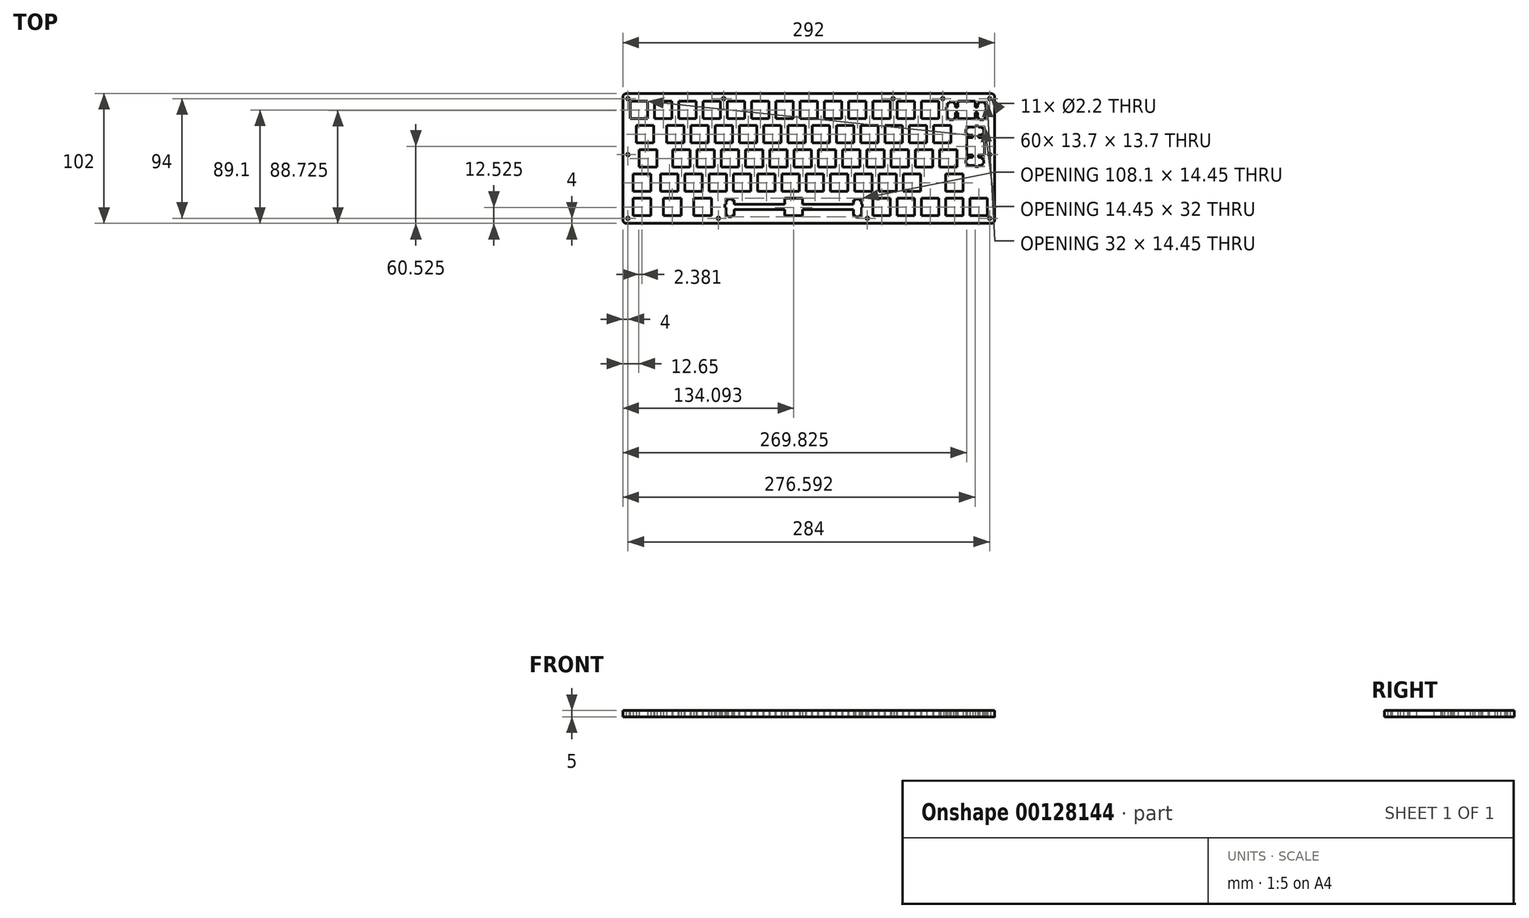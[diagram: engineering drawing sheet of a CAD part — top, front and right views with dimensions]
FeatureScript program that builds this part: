
annotation { "Feature Type Name" : "Feature", "Feature Type Description" : "" }
export const myFeature = defineFeature(function(context is Context, id is Id, definition is map)
    precondition{}
    {
        {
            var Q0;
            Q0=qCreatedBy(makeId("Top.planeOp"),FACE);
            var sketch = newSketch(context, id + "F0", { "sketchPlane" : qUnion([Q0])});
            skLineSegment(sketch, "E0", {"start": v(-18.76, -31.25) * mm, "end": v(-18.76, -35.95) * mm});
            skLineSegment(sketch, "E1", {"start": v(-18.76, -35.95) * mm, "end": v(-58.73, -35.95) * mm});
            skLineSegment(sketch, "E2", {"start": v(-58.73, -35.95) * mm, "end": v(-58.73, -32.72) * mm});
            skLineSegment(sketch, "E3", {"start": v(-58.73, -32.72) * mm, "end": v(-60.4, -32.72) * mm});
            skLineSegment(sketch, "E4", {"start": v(-60.4, -32.72) * mm, "end": v(-60.4, -31.8) * mm});
            skLineSegment(sketch, "E5", {"start": v(-60.4, -31.8) * mm, "end": v(-63.4, -31.8) * mm});
            skLineSegment(sketch, "E6", {"start": v(-63.4, -31.8) * mm, "end": v(-63.4, -32.72) * mm});
            skLineSegment(sketch, "E7", {"start": v(-63.4, -32.72) * mm, "end": v(-65.08, -32.72) * mm});
            skLineSegment(sketch, "E8", {"start": v(-65.08, -32.72) * mm, "end": v(-65.08, -35.95) * mm});
            skLineSegment(sketch, "E9", {"start": v(-65.08, -35.95) * mm, "end": v(-65.96, -35.95) * mm});
            skLineSegment(sketch, "E10", {"start": v(-65.96, -35.95) * mm, "end": v(-65.96, -38.45) * mm});
            skLineSegment(sketch, "E11", {"start": v(-65.96, -38.45) * mm, "end": v(-65.08, -38.45) * mm});
            skLineSegment(sketch, "E12", {"start": v(-65.08, -38.45) * mm, "end": v(-65.08, -44.72) * mm});
            skLineSegment(sketch, "E13", {"start": v(-65.08, -44.72) * mm, "end": v(-63.4, -44.72) * mm});
            skLineSegment(sketch, "E14", {"start": v(-63.4, -44.72) * mm, "end": v(-63.4, -45.7) * mm});
            skLineSegment(sketch, "E15", {"start": v(-63.4, -45.7) * mm, "end": v(-60.4, -45.7) * mm});
            skLineSegment(sketch, "E16", {"start": v(-60.4, -45.7) * mm, "end": v(-60.4, -44.72) * mm});
            skLineSegment(sketch, "E17", {"start": v(-60.4, -44.72) * mm, "end": v(-58.73, -44.72) * mm});
            skLineSegment(sketch, "E18", {"start": v(-58.73, -44.72) * mm, "end": v(-58.73, -40.25) * mm});
            skLineSegment(sketch, "E19", {"start": v(-58.73, -40.25) * mm, "end": v(-18.76, -40.25) * mm});
            skLineSegment(sketch, "E20", {"start": v(-18.76, -40.25) * mm, "end": v(-18.76, -44.95) * mm});
            skLineSegment(sketch, "E21", {"start": v(-18.76, -44.95) * mm, "end": v(-5.06, -44.95) * mm});
            skLineSegment(sketch, "E22", {"start": v(-5.06, -44.95) * mm, "end": v(-5.06, -40.25) * mm});
            skLineSegment(sketch, "E23", {"start": v(-5.06, -40.25) * mm, "end": v(34.92, -40.25) * mm});
            skLineSegment(sketch, "E24", {"start": v(34.92, -40.25) * mm, "end": v(34.92, -44.72) * mm});
            skLineSegment(sketch, "E25", {"start": v(34.92, -44.72) * mm, "end": v(36.6, -44.72) * mm});
            skLineSegment(sketch, "E26", {"start": v(36.6, -44.72) * mm, "end": v(36.6, -45.7) * mm});
            skLineSegment(sketch, "E27", {"start": v(36.6, -45.7) * mm, "end": v(39.6, -45.7) * mm});
            skLineSegment(sketch, "E28", {"start": v(39.6, -45.7) * mm, "end": v(39.6, -44.72) * mm});
            skLineSegment(sketch, "E29", {"start": v(39.6, -44.72) * mm, "end": v(41.27, -44.72) * mm});
            skLineSegment(sketch, "E30", {"start": v(41.27, -44.72) * mm, "end": v(41.27, -38.45) * mm});
            skLineSegment(sketch, "E31", {"start": v(41.27, -38.45) * mm, "end": v(42.14, -38.45) * mm});
            skLineSegment(sketch, "E32", {"start": v(42.14, -38.45) * mm, "end": v(42.14, -35.95) * mm});
            skLineSegment(sketch, "E33", {"start": v(42.14, -35.95) * mm, "end": v(41.27, -35.95) * mm});
            skLineSegment(sketch, "E34", {"start": v(41.27, -35.95) * mm, "end": v(41.27, -32.72) * mm});
            skLineSegment(sketch, "E35", {"start": v(41.27, -32.72) * mm, "end": v(39.6, -32.72) * mm});
            skLineSegment(sketch, "E36", {"start": v(39.6, -32.72) * mm, "end": v(39.6, -31.8) * mm});
            skLineSegment(sketch, "E37", {"start": v(39.6, -31.8) * mm, "end": v(36.6, -31.8) * mm});
            skLineSegment(sketch, "E38", {"start": v(36.6, -31.8) * mm, "end": v(36.6, -32.72) * mm});
            skLineSegment(sketch, "E39", {"start": v(36.6, -32.72) * mm, "end": v(34.92, -32.72) * mm});
            skLineSegment(sketch, "E40", {"start": v(34.92, -32.72) * mm, "end": v(34.92, -35.95) * mm});
            skLineSegment(sketch, "E41", {"start": v(34.92, -35.95) * mm, "end": v(-5.06, -35.95) * mm});
            skLineSegment(sketch, "E42", {"start": v(-5.06, -35.95) * mm, "end": v(-5.06, -31.25) * mm});
            skLineSegment(sketch, "E43", {"start": v(-5.06, -31.25) * mm, "end": v(-18.76, -31.25) * mm});
            skLineSegment(sketch, "E44", {"start": v(-137.82, -31.25) * mm, "end": v(-124.12, -31.25) * mm});
            skLineSegment(sketch, "E45", {"start": v(-124.12, -31.25) * mm, "end": v(-124.12, -44.95) * mm});
            skLineSegment(sketch, "E46", {"start": v(-124.12, -44.95) * mm, "end": v(-137.82, -44.95) * mm});
            skLineSegment(sketch, "E47", {"start": v(-137.82, -44.95) * mm, "end": v(-137.82, -31.25) * mm});
            skLineSegment(sketch, "E48", {"start": v(-114, -31.25) * mm, "end": v(-100.3, -31.25) * mm});
            skLineSegment(sketch, "E49", {"start": v(-100.3, -31.25) * mm, "end": v(-100.3, -44.95) * mm});
            skLineSegment(sketch, "E50", {"start": v(-100.3, -44.95) * mm, "end": v(-114, -44.95) * mm});
            skLineSegment(sketch, "E51", {"start": v(-114, -44.95) * mm, "end": v(-114, -31.25) * mm});
            skLineSegment(sketch, "E52", {"start": v(-90.2, -31.25) * mm, "end": v(-76.5, -31.25) * mm});
            skLineSegment(sketch, "E53", {"start": v(-76.5, -31.25) * mm, "end": v(-76.5, -44.95) * mm});
            skLineSegment(sketch, "E54", {"start": v(-76.5, -44.95) * mm, "end": v(-90.2, -44.95) * mm});
            skLineSegment(sketch, "E55", {"start": v(-90.2, -44.95) * mm, "end": v(-90.2, -31.25) * mm});
            skLineSegment(sketch, "E56", {"start": v(50.3, -31.25) * mm, "end": v(64, -31.25) * mm});
            skLineSegment(sketch, "E57", {"start": v(64, -31.25) * mm, "end": v(64, -44.95) * mm});
            skLineSegment(sketch, "E58", {"start": v(64, -44.95) * mm, "end": v(50.3, -44.95) * mm});
            skLineSegment(sketch, "E59", {"start": v(50.3, -44.95) * mm, "end": v(50.3, -31.25) * mm});
            skLineSegment(sketch, "E60", {"start": v(69.35, -31.25) * mm, "end": v(83.05, -31.25) * mm});
            skLineSegment(sketch, "E61", {"start": v(83.05, -31.25) * mm, "end": v(83.05, -44.95) * mm});
            skLineSegment(sketch, "E62", {"start": v(83.05, -44.95) * mm, "end": v(69.35, -44.95) * mm});
            skLineSegment(sketch, "E63", {"start": v(69.35, -44.95) * mm, "end": v(69.35, -31.25) * mm});
            skLineSegment(sketch, "E64", {"start": v(88.4, -31.25) * mm, "end": v(102.1, -31.25) * mm});
            skLineSegment(sketch, "E65", {"start": v(102.1, -31.25) * mm, "end": v(102.1, -44.95) * mm});
            skLineSegment(sketch, "E66", {"start": v(102.1, -44.95) * mm, "end": v(88.4, -44.95) * mm});
            skLineSegment(sketch, "E67", {"start": v(88.4, -44.95) * mm, "end": v(88.4, -31.25) * mm});
            skLineSegment(sketch, "E68", {"start": v(107.45, -31.25) * mm, "end": v(121.15, -31.25) * mm});
            skLineSegment(sketch, "E69", {"start": v(121.15, -31.25) * mm, "end": v(121.15, -44.95) * mm});
            skLineSegment(sketch, "E70", {"start": v(121.15, -44.95) * mm, "end": v(107.45, -44.95) * mm});
            skLineSegment(sketch, "E71", {"start": v(107.45, -44.95) * mm, "end": v(107.45, -31.25) * mm});
            skLineSegment(sketch, "E72", {"start": v(126.5, -31.25) * mm, "end": v(140.2, -31.25) * mm});
            skLineSegment(sketch, "E73", {"start": v(140.2, -31.25) * mm, "end": v(140.2, -44.95) * mm});
            skLineSegment(sketch, "E74", {"start": v(140.2, -44.95) * mm, "end": v(126.5, -44.95) * mm});
            skLineSegment(sketch, "E75", {"start": v(126.5, -44.95) * mm, "end": v(126.5, -31.25) * mm});
            skLineSegment(sketch, "E76", {"start": v(-137.82, -12.2) * mm, "end": v(-124.12, -12.2) * mm});
            skLineSegment(sketch, "E77", {"start": v(-124.12, -12.2) * mm, "end": v(-124.12, -25.9) * mm});
            skLineSegment(sketch, "E78", {"start": v(-124.12, -25.9) * mm, "end": v(-137.82, -25.9) * mm});
            skLineSegment(sketch, "E79", {"start": v(-137.82, -25.9) * mm, "end": v(-137.82, -12.2) * mm});
            skLineSegment(sketch, "E80", {"start": v(-116.39, -12.2) * mm, "end": v(-102.69, -12.2) * mm});
            skLineSegment(sketch, "E81", {"start": v(-102.69, -12.2) * mm, "end": v(-102.69, -25.9) * mm});
            skLineSegment(sketch, "E82", {"start": v(-102.69, -25.9) * mm, "end": v(-116.39, -25.9) * mm});
            skLineSegment(sketch, "E83", {"start": v(-116.39, -25.9) * mm, "end": v(-116.39, -12.2) * mm});
            skLineSegment(sketch, "E84", {"start": v(-97.34, -12.2) * mm, "end": v(-83.64, -12.2) * mm});
            skLineSegment(sketch, "E85", {"start": v(-83.64, -12.2) * mm, "end": v(-83.64, -25.9) * mm});
            skLineSegment(sketch, "E86", {"start": v(-83.64, -25.9) * mm, "end": v(-97.34, -25.9) * mm});
            skLineSegment(sketch, "E87", {"start": v(-97.34, -25.9) * mm, "end": v(-97.34, -12.2) * mm});
            skLineSegment(sketch, "E88", {"start": v(-78.29, -12.2) * mm, "end": v(-64.59, -12.2) * mm});
            skLineSegment(sketch, "E89", {"start": v(-64.59, -12.2) * mm, "end": v(-64.59, -25.9) * mm});
            skLineSegment(sketch, "E90", {"start": v(-64.59, -25.9) * mm, "end": v(-78.29, -25.9) * mm});
            skLineSegment(sketch, "E91", {"start": v(-78.29, -25.9) * mm, "end": v(-78.29, -12.2) * mm});
            skLineSegment(sketch, "E92", {"start": v(-59.24, -12.2) * mm, "end": v(-45.54, -12.2) * mm});
            skLineSegment(sketch, "E93", {"start": v(-45.54, -12.2) * mm, "end": v(-45.54, -25.9) * mm});
            skLineSegment(sketch, "E94", {"start": v(-45.54, -25.9) * mm, "end": v(-59.24, -25.9) * mm});
            skLineSegment(sketch, "E95", {"start": v(-59.24, -25.9) * mm, "end": v(-59.24, -12.2) * mm});
            skLineSegment(sketch, "E96", {"start": v(-40.19, -12.2) * mm, "end": v(-26.49, -12.2) * mm});
            skLineSegment(sketch, "E97", {"start": v(-26.49, -12.2) * mm, "end": v(-26.49, -25.9) * mm});
            skLineSegment(sketch, "E98", {"start": v(-26.49, -25.9) * mm, "end": v(-40.19, -25.9) * mm});
            skLineSegment(sketch, "E99", {"start": v(-40.19, -25.9) * mm, "end": v(-40.19, -12.2) * mm});
            skLineSegment(sketch, "E100", {"start": v(-21.14, -12.2) * mm, "end": v(-7.44, -12.2) * mm});
            skLineSegment(sketch, "E101", {"start": v(-7.44, -12.2) * mm, "end": v(-7.44, -25.9) * mm});
            skLineSegment(sketch, "E102", {"start": v(-7.44, -25.9) * mm, "end": v(-21.14, -25.9) * mm});
            skLineSegment(sketch, "E103", {"start": v(-21.14, -25.9) * mm, "end": v(-21.14, -12.2) * mm});
            skLineSegment(sketch, "E104", {"start": v(-2.09, -12.2) * mm, "end": v(11.61, -12.2) * mm});
            skLineSegment(sketch, "E105", {"start": v(11.61, -12.2) * mm, "end": v(11.61, -25.9) * mm});
            skLineSegment(sketch, "E106", {"start": v(11.61, -25.9) * mm, "end": v(-2.09, -25.9) * mm});
            skLineSegment(sketch, "E107", {"start": v(-2.09, -25.9) * mm, "end": v(-2.09, -12.2) * mm});
            skLineSegment(sketch, "E108", {"start": v(16.96, -12.2) * mm, "end": v(30.66, -12.2) * mm});
            skLineSegment(sketch, "E109", {"start": v(30.66, -12.2) * mm, "end": v(30.66, -25.9) * mm});
            skLineSegment(sketch, "E110", {"start": v(30.66, -25.9) * mm, "end": v(16.96, -25.9) * mm});
            skLineSegment(sketch, "E111", {"start": v(16.96, -25.9) * mm, "end": v(16.96, -12.2) * mm});
            skLineSegment(sketch, "E112", {"start": v(36.01, -12.2) * mm, "end": v(49.71, -12.2) * mm});
            skLineSegment(sketch, "E113", {"start": v(49.71, -12.2) * mm, "end": v(49.71, -25.9) * mm});
            skLineSegment(sketch, "E114", {"start": v(49.71, -25.9) * mm, "end": v(36.01, -25.9) * mm});
            skLineSegment(sketch, "E115", {"start": v(36.01, -25.9) * mm, "end": v(36.01, -12.2) * mm});
            skLineSegment(sketch, "E116", {"start": v(55.06, -12.2) * mm, "end": v(68.76, -12.2) * mm});
            skLineSegment(sketch, "E117", {"start": v(68.76, -12.2) * mm, "end": v(68.76, -25.9) * mm});
            skLineSegment(sketch, "E118", {"start": v(68.76, -25.9) * mm, "end": v(55.06, -25.9) * mm});
            skLineSegment(sketch, "E119", {"start": v(55.06, -25.9) * mm, "end": v(55.06, -12.2) * mm});
            skLineSegment(sketch, "E120", {"start": v(74.11, -12.2) * mm, "end": v(87.81, -12.2) * mm});
            skLineSegment(sketch, "E121", {"start": v(87.81, -12.2) * mm, "end": v(87.81, -25.9) * mm});
            skLineSegment(sketch, "E122", {"start": v(87.81, -25.9) * mm, "end": v(74.11, -25.9) * mm});
            skLineSegment(sketch, "E123", {"start": v(74.11, -25.9) * mm, "end": v(74.11, -12.2) * mm});
            skLineSegment(sketch, "E124", {"start": v(107.45, -12.2) * mm, "end": v(121.15, -12.2) * mm});
            skLineSegment(sketch, "E125", {"start": v(121.15, -12.2) * mm, "end": v(121.15, -25.9) * mm});
            skLineSegment(sketch, "E126", {"start": v(121.15, -25.9) * mm, "end": v(107.45, -25.9) * mm});
            skLineSegment(sketch, "E127", {"start": v(107.45, -25.9) * mm, "end": v(107.45, -12.2) * mm});
            skLineSegment(sketch, "E128", {"start": v(-133.06, 6.85) * mm, "end": v(-119.36, 6.85) * mm});
            skLineSegment(sketch, "E129", {"start": v(-119.36, 6.85) * mm, "end": v(-119.36, -6.85) * mm});
            skLineSegment(sketch, "E130", {"start": v(-119.36, -6.85) * mm, "end": v(-133.06, -6.85) * mm});
            skLineSegment(sketch, "E131", {"start": v(-133.06, -6.85) * mm, "end": v(-133.06, 6.85) * mm});
            skLineSegment(sketch, "E132", {"start": v(-106.86, 6.85) * mm, "end": v(-93.16, 6.85) * mm});
            skLineSegment(sketch, "E133", {"start": v(-93.16, 6.85) * mm, "end": v(-93.16, -6.85) * mm});
            skLineSegment(sketch, "E134", {"start": v(-93.16, -6.85) * mm, "end": v(-106.86, -6.85) * mm});
            skLineSegment(sketch, "E135", {"start": v(-106.86, -6.85) * mm, "end": v(-106.86, 6.85) * mm});
            skLineSegment(sketch, "E136", {"start": v(-87.81, 6.85) * mm, "end": v(-74.11, 6.85) * mm});
            skLineSegment(sketch, "E137", {"start": v(-74.11, 6.85) * mm, "end": v(-74.11, -6.85) * mm});
            skLineSegment(sketch, "E138", {"start": v(-74.11, -6.85) * mm, "end": v(-87.81, -6.85) * mm});
            skLineSegment(sketch, "E139", {"start": v(-87.81, -6.85) * mm, "end": v(-87.81, 6.85) * mm});
            skLineSegment(sketch, "E140", {"start": v(-68.76, 6.85) * mm, "end": v(-55.06, 6.85) * mm});
            skLineSegment(sketch, "E141", {"start": v(-55.06, 6.85) * mm, "end": v(-55.06, -6.85) * mm});
            skLineSegment(sketch, "E142", {"start": v(-55.06, -6.85) * mm, "end": v(-68.76, -6.85) * mm});
            skLineSegment(sketch, "E143", {"start": v(-68.76, -6.85) * mm, "end": v(-68.76, 6.85) * mm});
            skLineSegment(sketch, "E144", {"start": v(-49.71, 6.85) * mm, "end": v(-36.01, 6.85) * mm});
            skLineSegment(sketch, "E145", {"start": v(-36.01, 6.85) * mm, "end": v(-36.01, -6.85) * mm});
            skLineSegment(sketch, "E146", {"start": v(-36.01, -6.85) * mm, "end": v(-49.71, -6.85) * mm});
            skLineSegment(sketch, "E147", {"start": v(-49.71, -6.85) * mm, "end": v(-49.71, 6.85) * mm});
            skLineSegment(sketch, "E148", {"start": v(-30.66, 6.85) * mm, "end": v(-16.96, 6.85) * mm});
            skLineSegment(sketch, "E149", {"start": v(-16.96, 6.85) * mm, "end": v(-16.96, -6.85) * mm});
            skLineSegment(sketch, "E150", {"start": v(-16.96, -6.85) * mm, "end": v(-30.66, -6.85) * mm});
            skLineSegment(sketch, "E151", {"start": v(-30.66, -6.85) * mm, "end": v(-30.66, 6.85) * mm});
            skLineSegment(sketch, "E152", {"start": v(-11.61, 6.85) * mm, "end": v(2.09, 6.85) * mm});
            skLineSegment(sketch, "E153", {"start": v(2.09, 6.85) * mm, "end": v(2.09, -6.85) * mm});
            skLineSegment(sketch, "E154", {"start": v(2.09, -6.85) * mm, "end": v(-11.61, -6.85) * mm});
            skLineSegment(sketch, "E155", {"start": v(-11.61, -6.85) * mm, "end": v(-11.61, 6.85) * mm});
            skLineSegment(sketch, "E156", {"start": v(7.44, 6.85) * mm, "end": v(21.14, 6.85) * mm});
            skLineSegment(sketch, "E157", {"start": v(21.14, 6.85) * mm, "end": v(21.14, -6.85) * mm});
            skLineSegment(sketch, "E158", {"start": v(21.14, -6.85) * mm, "end": v(7.44, -6.85) * mm});
            skLineSegment(sketch, "E159", {"start": v(7.44, -6.85) * mm, "end": v(7.44, 6.85) * mm});
            skLineSegment(sketch, "E160", {"start": v(26.49, 6.85) * mm, "end": v(40.19, 6.85) * mm});
            skLineSegment(sketch, "E161", {"start": v(40.19, 6.85) * mm, "end": v(40.19, -6.85) * mm});
            skLineSegment(sketch, "E162", {"start": v(40.19, -6.85) * mm, "end": v(26.49, -6.85) * mm});
            skLineSegment(sketch, "E163", {"start": v(26.49, -6.85) * mm, "end": v(26.49, 6.85) * mm});
            skLineSegment(sketch, "E164", {"start": v(45.54, 6.85) * mm, "end": v(59.24, 6.85) * mm});
            skLineSegment(sketch, "E165", {"start": v(59.24, 6.85) * mm, "end": v(59.24, -6.85) * mm});
            skLineSegment(sketch, "E166", {"start": v(59.24, -6.85) * mm, "end": v(45.54, -6.85) * mm});
            skLineSegment(sketch, "E167", {"start": v(45.54, -6.85) * mm, "end": v(45.54, 6.85) * mm});
            skLineSegment(sketch, "E168", {"start": v(64.59, 6.85) * mm, "end": v(78.29, 6.85) * mm});
            skLineSegment(sketch, "E169", {"start": v(78.29, 6.85) * mm, "end": v(78.29, -6.85) * mm});
            skLineSegment(sketch, "E170", {"start": v(78.29, -6.85) * mm, "end": v(64.59, -6.85) * mm});
            skLineSegment(sketch, "E171", {"start": v(64.59, -6.85) * mm, "end": v(64.59, 6.85) * mm});
            skLineSegment(sketch, "E172", {"start": v(83.64, 6.85) * mm, "end": v(97.34, 6.85) * mm});
            skLineSegment(sketch, "E173", {"start": v(97.34, 6.85) * mm, "end": v(97.34, -6.85) * mm});
            skLineSegment(sketch, "E174", {"start": v(97.34, -6.85) * mm, "end": v(83.64, -6.85) * mm});
            skLineSegment(sketch, "E175", {"start": v(83.64, -6.85) * mm, "end": v(83.64, 6.85) * mm});
            skLineSegment(sketch, "E176", {"start": v(102.69, 6.85) * mm, "end": v(116.39, 6.85) * mm});
            skLineSegment(sketch, "E177", {"start": v(116.39, 6.85) * mm, "end": v(116.39, -6.85) * mm});
            skLineSegment(sketch, "E178", {"start": v(116.39, -6.85) * mm, "end": v(102.69, -6.85) * mm});
            skLineSegment(sketch, "E179", {"start": v(102.69, -6.85) * mm, "end": v(102.69, 6.85) * mm});
            skLineSegment(sketch, "E180", {"start": v(130.62, 25.53) * mm, "end": v(130.62, 24.65) * mm});
            skLineSegment(sketch, "E181", {"start": v(130.62, 24.65) * mm, "end": v(124.35, 24.65) * mm});
            skLineSegment(sketch, "E182", {"start": v(124.35, 24.65) * mm, "end": v(124.35, 22.97) * mm});
            skLineSegment(sketch, "E183", {"start": v(124.35, 22.97) * mm, "end": v(123.37, 22.97) * mm});
            skLineSegment(sketch, "E184", {"start": v(123.37, 22.97) * mm, "end": v(123.37, 19.98) * mm});
            skLineSegment(sketch, "E185", {"start": v(123.37, 19.98) * mm, "end": v(124.35, 19.98) * mm});
            skLineSegment(sketch, "E186", {"start": v(124.35, 19.98) * mm, "end": v(124.35, 18.3) * mm});
            skLineSegment(sketch, "E187", {"start": v(124.35, 18.3) * mm, "end": v(128.82, 18.3) * mm});
            skLineSegment(sketch, "E188", {"start": v(128.82, 18.3) * mm, "end": v(128.82, 16.38) * mm});
            skLineSegment(sketch, "E189", {"start": v(128.82, 16.38) * mm, "end": v(124.12, 16.38) * mm});
            skLineSegment(sketch, "E190", {"start": v(124.12, 16.38) * mm, "end": v(124.12, 2.68) * mm});
            skLineSegment(sketch, "E191", {"start": v(124.12, 2.68) * mm, "end": v(128.82, 2.68) * mm});
            skLineSegment(sketch, "E192", {"start": v(128.82, 2.68) * mm, "end": v(128.82, 0.75) * mm});
            skLineSegment(sketch, "E193", {"start": v(128.82, 0.75) * mm, "end": v(124.35, 0.75) * mm});
            skLineSegment(sketch, "E194", {"start": v(124.35, 0.75) * mm, "end": v(124.35, -0.92) * mm});
            skLineSegment(sketch, "E195", {"start": v(124.35, -0.92) * mm, "end": v(123.37, -0.92) * mm});
            skLineSegment(sketch, "E196", {"start": v(123.37, -0.92) * mm, "end": v(123.37, -3.92) * mm});
            skLineSegment(sketch, "E197", {"start": v(123.37, -3.92) * mm, "end": v(124.35, -3.92) * mm});
            skLineSegment(sketch, "E198", {"start": v(124.35, -3.92) * mm, "end": v(124.35, -5.6) * mm});
            skLineSegment(sketch, "E199", {"start": v(124.35, -5.6) * mm, "end": v(130.62, -5.6) * mm});
            skLineSegment(sketch, "E200", {"start": v(130.62, -5.6) * mm, "end": v(130.62, -6.48) * mm});
            skLineSegment(sketch, "E201", {"start": v(130.62, -6.48) * mm, "end": v(133.12, -6.48) * mm});
            skLineSegment(sketch, "E202", {"start": v(133.12, -6.48) * mm, "end": v(133.12, -5.6) * mm});
            skLineSegment(sketch, "E203", {"start": v(133.12, -5.6) * mm, "end": v(136.35, -5.6) * mm});
            skLineSegment(sketch, "E204", {"start": v(136.35, -5.6) * mm, "end": v(136.35, -3.92) * mm});
            skLineSegment(sketch, "E205", {"start": v(136.35, -3.92) * mm, "end": v(137.27, -3.92) * mm});
            skLineSegment(sketch, "E206", {"start": v(137.27, -3.92) * mm, "end": v(137.27, -0.92) * mm});
            skLineSegment(sketch, "E207", {"start": v(137.27, -0.92) * mm, "end": v(136.35, -0.92) * mm});
            skLineSegment(sketch, "E208", {"start": v(136.35, -0.92) * mm, "end": v(136.35, 0.75) * mm});
            skLineSegment(sketch, "E209", {"start": v(136.35, 0.75) * mm, "end": v(133.12, 0.75) * mm});
            skLineSegment(sketch, "E210", {"start": v(133.12, 0.75) * mm, "end": v(133.12, 2.68) * mm});
            skLineSegment(sketch, "E211", {"start": v(133.12, 2.68) * mm, "end": v(137.82, 2.68) * mm});
            skLineSegment(sketch, "E212", {"start": v(137.82, 2.68) * mm, "end": v(137.82, 16.38) * mm});
            skLineSegment(sketch, "E213", {"start": v(137.82, 16.38) * mm, "end": v(133.12, 16.38) * mm});
            skLineSegment(sketch, "E214", {"start": v(133.12, 16.38) * mm, "end": v(133.12, 18.3) * mm});
            skLineSegment(sketch, "E215", {"start": v(133.12, 18.3) * mm, "end": v(136.35, 18.3) * mm});
            skLineSegment(sketch, "E216", {"start": v(136.35, 18.3) * mm, "end": v(136.35, 19.98) * mm});
            skLineSegment(sketch, "E217", {"start": v(136.35, 19.98) * mm, "end": v(137.27, 19.98) * mm});
            skLineSegment(sketch, "E218", {"start": v(137.27, 19.98) * mm, "end": v(137.27, 22.97) * mm});
            skLineSegment(sketch, "E219", {"start": v(137.27, 22.97) * mm, "end": v(136.35, 22.97) * mm});
            skLineSegment(sketch, "E220", {"start": v(136.35, 22.97) * mm, "end": v(136.35, 24.65) * mm});
            skLineSegment(sketch, "E221", {"start": v(136.35, 24.65) * mm, "end": v(133.12, 24.65) * mm});
            skLineSegment(sketch, "E222", {"start": v(133.12, 24.65) * mm, "end": v(133.12, 25.53) * mm});
            skLineSegment(sketch, "E223", {"start": v(133.12, 25.53) * mm, "end": v(130.62, 25.53) * mm});
            skLineSegment(sketch, "E224", {"start": v(-135.44, 25.9) * mm, "end": v(-121.74, 25.9) * mm});
            skLineSegment(sketch, "E225", {"start": v(-121.74, 25.9) * mm, "end": v(-121.74, 12.2) * mm});
            skLineSegment(sketch, "E226", {"start": v(-121.74, 12.2) * mm, "end": v(-135.44, 12.2) * mm});
            skLineSegment(sketch, "E227", {"start": v(-135.44, 12.2) * mm, "end": v(-135.44, 25.9) * mm});
            skLineSegment(sketch, "E228", {"start": v(-111.63, 25.9) * mm, "end": v(-97.92, 25.9) * mm});
            skLineSegment(sketch, "E229", {"start": v(-97.92, 25.9) * mm, "end": v(-97.92, 12.2) * mm});
            skLineSegment(sketch, "E230", {"start": v(-97.92, 12.2) * mm, "end": v(-111.63, 12.2) * mm});
            skLineSegment(sketch, "E231", {"start": v(-111.63, 12.2) * mm, "end": v(-111.63, 25.9) * mm});
            skLineSegment(sketch, "E232", {"start": v(-92.58, 25.9) * mm, "end": v(-78.88, 25.9) * mm});
            skLineSegment(sketch, "E233", {"start": v(-78.88, 25.9) * mm, "end": v(-78.88, 12.2) * mm});
            skLineSegment(sketch, "E234", {"start": v(-78.88, 12.2) * mm, "end": v(-92.58, 12.2) * mm});
            skLineSegment(sketch, "E235", {"start": v(-92.58, 12.2) * mm, "end": v(-92.58, 25.9) * mm});
            skLineSegment(sketch, "E236", {"start": v(-73.53, 25.9) * mm, "end": v(-59.83, 25.9) * mm});
            skLineSegment(sketch, "E237", {"start": v(-59.83, 25.9) * mm, "end": v(-59.83, 12.2) * mm});
            skLineSegment(sketch, "E238", {"start": v(-59.83, 12.2) * mm, "end": v(-73.53, 12.2) * mm});
            skLineSegment(sketch, "E239", {"start": v(-73.53, 12.2) * mm, "end": v(-73.53, 25.9) * mm});
            skLineSegment(sketch, "E240", {"start": v(-54.48, 25.9) * mm, "end": v(-40.78, 25.9) * mm});
            skLineSegment(sketch, "E241", {"start": v(-40.78, 25.9) * mm, "end": v(-40.78, 12.2) * mm});
            skLineSegment(sketch, "E242", {"start": v(-40.78, 12.2) * mm, "end": v(-54.48, 12.2) * mm});
            skLineSegment(sketch, "E243", {"start": v(-54.48, 12.2) * mm, "end": v(-54.48, 25.9) * mm});
            skLineSegment(sketch, "E244", {"start": v(-35.42, 25.9) * mm, "end": v(-21.73, 25.9) * mm});
            skLineSegment(sketch, "E245", {"start": v(-21.73, 25.9) * mm, "end": v(-21.73, 12.2) * mm});
            skLineSegment(sketch, "E246", {"start": v(-21.73, 12.2) * mm, "end": v(-35.42, 12.2) * mm});
            skLineSegment(sketch, "E247", {"start": v(-35.42, 12.2) * mm, "end": v(-35.42, 25.9) * mm});
            skLineSegment(sketch, "E248", {"start": v(-16.37, 25.9) * mm, "end": v(-2.67, 25.9) * mm});
            skLineSegment(sketch, "E249", {"start": v(-2.67, 25.9) * mm, "end": v(-2.67, 12.2) * mm});
            skLineSegment(sketch, "E250", {"start": v(-2.67, 12.2) * mm, "end": v(-16.37, 12.2) * mm});
            skLineSegment(sketch, "E251", {"start": v(-16.37, 12.2) * mm, "end": v(-16.37, 25.9) * mm});
            skLineSegment(sketch, "E252", {"start": v(2.68, 25.9) * mm, "end": v(16.38, 25.9) * mm});
            skLineSegment(sketch, "E253", {"start": v(16.38, 25.9) * mm, "end": v(16.38, 12.2) * mm});
            skLineSegment(sketch, "E254", {"start": v(16.38, 12.2) * mm, "end": v(2.68, 12.2) * mm});
            skLineSegment(sketch, "E255", {"start": v(2.68, 12.2) * mm, "end": v(2.68, 25.9) * mm});
            skLineSegment(sketch, "E256", {"start": v(21.73, 25.9) * mm, "end": v(35.43, 25.9) * mm});
            skLineSegment(sketch, "E257", {"start": v(35.43, 25.9) * mm, "end": v(35.43, 12.2) * mm});
            skLineSegment(sketch, "E258", {"start": v(35.43, 12.2) * mm, "end": v(21.73, 12.2) * mm});
            skLineSegment(sketch, "E259", {"start": v(21.73, 12.2) * mm, "end": v(21.73, 25.9) * mm});
            skLineSegment(sketch, "E260", {"start": v(40.78, 25.9) * mm, "end": v(54.48, 25.9) * mm});
            skLineSegment(sketch, "E261", {"start": v(54.48, 25.9) * mm, "end": v(54.48, 12.2) * mm});
            skLineSegment(sketch, "E262", {"start": v(54.48, 12.2) * mm, "end": v(40.78, 12.2) * mm});
            skLineSegment(sketch, "E263", {"start": v(40.78, 12.2) * mm, "end": v(40.78, 25.9) * mm});
            skLineSegment(sketch, "E264", {"start": v(59.83, 25.9) * mm, "end": v(73.53, 25.9) * mm});
            skLineSegment(sketch, "E265", {"start": v(73.53, 25.9) * mm, "end": v(73.53, 12.2) * mm});
            skLineSegment(sketch, "E266", {"start": v(73.53, 12.2) * mm, "end": v(59.83, 12.2) * mm});
            skLineSegment(sketch, "E267", {"start": v(59.83, 12.2) * mm, "end": v(59.83, 25.9) * mm});
            skLineSegment(sketch, "E268", {"start": v(78.88, 25.9) * mm, "end": v(92.58, 25.9) * mm});
            skLineSegment(sketch, "E269", {"start": v(92.58, 25.9) * mm, "end": v(92.58, 12.2) * mm});
            skLineSegment(sketch, "E270", {"start": v(92.58, 12.2) * mm, "end": v(78.88, 12.2) * mm});
            skLineSegment(sketch, "E271", {"start": v(78.88, 12.2) * mm, "end": v(78.88, 25.9) * mm});
            skLineSegment(sketch, "E272", {"start": v(97.93, 25.9) * mm, "end": v(111.63, 25.9) * mm});
            skLineSegment(sketch, "E273", {"start": v(111.63, 25.9) * mm, "end": v(111.63, 12.2) * mm});
            skLineSegment(sketch, "E274", {"start": v(111.63, 12.2) * mm, "end": v(97.93, 12.2) * mm});
            skLineSegment(sketch, "E275", {"start": v(97.93, 12.2) * mm, "end": v(97.93, 25.9) * mm});
            skLineSegment(sketch, "E276", {"start": v(116.98, 44.95) * mm, "end": v(116.98, 40.25) * mm});
            skLineSegment(sketch, "E277", {"start": v(116.98, 40.25) * mm, "end": v(115.05, 40.25) * mm});
            skLineSegment(sketch, "E278", {"start": v(115.05, 40.25) * mm, "end": v(115.05, 43.48) * mm});
            skLineSegment(sketch, "E279", {"start": v(115.05, 43.48) * mm, "end": v(113.38, 43.48) * mm});
            skLineSegment(sketch, "E280", {"start": v(113.38, 43.48) * mm, "end": v(113.38, 44.4) * mm});
            skLineSegment(sketch, "E281", {"start": v(113.38, 44.4) * mm, "end": v(110.37, 44.4) * mm});
            skLineSegment(sketch, "E282", {"start": v(110.37, 44.4) * mm, "end": v(110.37, 43.48) * mm});
            skLineSegment(sketch, "E283", {"start": v(110.37, 43.48) * mm, "end": v(108.7, 43.48) * mm});
            skLineSegment(sketch, "E284", {"start": v(108.7, 43.48) * mm, "end": v(108.7, 40.25) * mm});
            skLineSegment(sketch, "E285", {"start": v(108.7, 40.25) * mm, "end": v(107.83, 40.25) * mm});
            skLineSegment(sketch, "E286", {"start": v(107.83, 40.25) * mm, "end": v(107.83, 37.75) * mm});
            skLineSegment(sketch, "E287", {"start": v(107.83, 37.75) * mm, "end": v(108.7, 37.75) * mm});
            skLineSegment(sketch, "E288", {"start": v(108.7, 37.75) * mm, "end": v(108.7, 31.48) * mm});
            skLineSegment(sketch, "E289", {"start": v(108.7, 31.48) * mm, "end": v(110.37, 31.48) * mm});
            skLineSegment(sketch, "E290", {"start": v(110.37, 31.48) * mm, "end": v(110.37, 30.5) * mm});
            skLineSegment(sketch, "E291", {"start": v(110.37, 30.5) * mm, "end": v(113.38, 30.5) * mm});
            skLineSegment(sketch, "E292", {"start": v(113.38, 30.5) * mm, "end": v(113.38, 31.48) * mm});
            skLineSegment(sketch, "E293", {"start": v(113.38, 31.48) * mm, "end": v(115.05, 31.48) * mm});
            skLineSegment(sketch, "E294", {"start": v(115.05, 31.48) * mm, "end": v(115.05, 35.95) * mm});
            skLineSegment(sketch, "E295", {"start": v(115.05, 35.95) * mm, "end": v(116.98, 35.95) * mm});
            skLineSegment(sketch, "E296", {"start": v(116.98, 35.95) * mm, "end": v(116.98, 31.25) * mm});
            skLineSegment(sketch, "E297", {"start": v(116.98, 31.25) * mm, "end": v(130.68, 31.25) * mm});
            skLineSegment(sketch, "E298", {"start": v(130.68, 31.25) * mm, "end": v(130.68, 35.95) * mm});
            skLineSegment(sketch, "E299", {"start": v(130.68, 35.95) * mm, "end": v(132.6, 35.95) * mm});
            skLineSegment(sketch, "E300", {"start": v(132.6, 35.95) * mm, "end": v(132.6, 31.48) * mm});
            skLineSegment(sketch, "E301", {"start": v(132.6, 31.48) * mm, "end": v(134.27, 31.48) * mm});
            skLineSegment(sketch, "E302", {"start": v(134.27, 31.48) * mm, "end": v(134.27, 30.5) * mm});
            skLineSegment(sketch, "E303", {"start": v(134.27, 30.5) * mm, "end": v(137.27, 30.5) * mm});
            skLineSegment(sketch, "E304", {"start": v(137.27, 30.5) * mm, "end": v(137.27, 31.48) * mm});
            skLineSegment(sketch, "E305", {"start": v(137.27, 31.48) * mm, "end": v(138.95, 31.48) * mm});
            skLineSegment(sketch, "E306", {"start": v(138.95, 31.48) * mm, "end": v(138.95, 37.75) * mm});
            skLineSegment(sketch, "E307", {"start": v(138.95, 37.75) * mm, "end": v(139.83, 37.75) * mm});
            skLineSegment(sketch, "E308", {"start": v(139.83, 37.75) * mm, "end": v(139.83, 40.25) * mm});
            skLineSegment(sketch, "E309", {"start": v(139.83, 40.25) * mm, "end": v(138.95, 40.25) * mm});
            skLineSegment(sketch, "E310", {"start": v(138.95, 40.25) * mm, "end": v(138.95, 43.48) * mm});
            skLineSegment(sketch, "E311", {"start": v(138.95, 43.48) * mm, "end": v(137.27, 43.48) * mm});
            skLineSegment(sketch, "E312", {"start": v(137.27, 43.48) * mm, "end": v(137.27, 44.4) * mm});
            skLineSegment(sketch, "E313", {"start": v(137.27, 44.4) * mm, "end": v(134.27, 44.4) * mm});
            skLineSegment(sketch, "E314", {"start": v(134.27, 44.4) * mm, "end": v(134.27, 43.48) * mm});
            skLineSegment(sketch, "E315", {"start": v(134.27, 43.48) * mm, "end": v(132.6, 43.48) * mm});
            skLineSegment(sketch, "E316", {"start": v(132.6, 43.48) * mm, "end": v(132.6, 40.25) * mm});
            skLineSegment(sketch, "E317", {"start": v(132.6, 40.25) * mm, "end": v(130.68, 40.25) * mm});
            skLineSegment(sketch, "E318", {"start": v(130.68, 40.25) * mm, "end": v(130.68, 44.95) * mm});
            skLineSegment(sketch, "E319", {"start": v(130.68, 44.95) * mm, "end": v(116.98, 44.95) * mm});
            skLineSegment(sketch, "E320", {"start": v(-140.2, 44.95) * mm, "end": v(-126.5, 44.95) * mm});
            skLineSegment(sketch, "E321", {"start": v(-126.5, 44.95) * mm, "end": v(-126.5, 31.25) * mm});
            skLineSegment(sketch, "E322", {"start": v(-126.5, 31.25) * mm, "end": v(-140.2, 31.25) * mm});
            skLineSegment(sketch, "E323", {"start": v(-140.2, 31.25) * mm, "end": v(-140.2, 44.95) * mm});
            skLineSegment(sketch, "E324", {"start": v(-121.15, 44.95) * mm, "end": v(-107.45, 44.95) * mm});
            skLineSegment(sketch, "E325", {"start": v(-107.45, 44.95) * mm, "end": v(-107.45, 31.25) * mm});
            skLineSegment(sketch, "E326", {"start": v(-107.45, 31.25) * mm, "end": v(-121.15, 31.25) * mm});
            skLineSegment(sketch, "E327", {"start": v(-121.15, 31.25) * mm, "end": v(-121.15, 44.95) * mm});
            skLineSegment(sketch, "E328", {"start": v(-102.1, 44.95) * mm, "end": v(-88.4, 44.95) * mm});
            skLineSegment(sketch, "E329", {"start": v(-88.4, 44.95) * mm, "end": v(-88.4, 31.25) * mm});
            skLineSegment(sketch, "E330", {"start": v(-88.4, 31.25) * mm, "end": v(-102.1, 31.25) * mm});
            skLineSegment(sketch, "E331", {"start": v(-102.1, 31.25) * mm, "end": v(-102.1, 44.95) * mm});
            skLineSegment(sketch, "E332", {"start": v(-83.05, 44.95) * mm, "end": v(-69.35, 44.95) * mm});
            skLineSegment(sketch, "E333", {"start": v(-69.35, 44.95) * mm, "end": v(-69.35, 31.25) * mm});
            skLineSegment(sketch, "E334", {"start": v(-69.35, 31.25) * mm, "end": v(-83.05, 31.25) * mm});
            skLineSegment(sketch, "E335", {"start": v(-83.05, 31.25) * mm, "end": v(-83.05, 44.95) * mm});
            skLineSegment(sketch, "E336", {"start": v(-64, 44.95) * mm, "end": v(-50.3, 44.95) * mm});
            skLineSegment(sketch, "E337", {"start": v(-50.3, 44.95) * mm, "end": v(-50.3, 31.25) * mm});
            skLineSegment(sketch, "E338", {"start": v(-50.3, 31.25) * mm, "end": v(-64, 31.25) * mm});
            skLineSegment(sketch, "E339", {"start": v(-64, 31.25) * mm, "end": v(-64, 44.95) * mm});
            skLineSegment(sketch, "E340", {"start": v(-44.95, 44.95) * mm, "end": v(-31.25, 44.95) * mm});
            skLineSegment(sketch, "E341", {"start": v(-31.25, 44.95) * mm, "end": v(-31.25, 31.25) * mm});
            skLineSegment(sketch, "E342", {"start": v(-31.25, 31.25) * mm, "end": v(-44.95, 31.25) * mm});
            skLineSegment(sketch, "E343", {"start": v(-44.95, 31.25) * mm, "end": v(-44.95, 44.95) * mm});
            skLineSegment(sketch, "E344", {"start": v(-25.9, 44.95) * mm, "end": v(-12.2, 44.95) * mm});
            skLineSegment(sketch, "E345", {"start": v(-12.2, 44.95) * mm, "end": v(-12.2, 31.25) * mm});
            skLineSegment(sketch, "E346", {"start": v(-12.2, 31.25) * mm, "end": v(-25.9, 31.25) * mm});
            skLineSegment(sketch, "E347", {"start": v(-25.9, 31.25) * mm, "end": v(-25.9, 44.95) * mm});
            skLineSegment(sketch, "E348", {"start": v(-6.85, 44.95) * mm, "end": v(6.85, 44.95) * mm});
            skLineSegment(sketch, "E349", {"start": v(6.85, 44.95) * mm, "end": v(6.85, 31.25) * mm});
            skLineSegment(sketch, "E350", {"start": v(6.85, 31.25) * mm, "end": v(-6.85, 31.25) * mm});
            skLineSegment(sketch, "E351", {"start": v(-6.85, 31.25) * mm, "end": v(-6.85, 44.95) * mm});
            skLineSegment(sketch, "E352", {"start": v(12.2, 44.95) * mm, "end": v(25.9, 44.95) * mm});
            skLineSegment(sketch, "E353", {"start": v(25.9, 44.95) * mm, "end": v(25.9, 31.25) * mm});
            skLineSegment(sketch, "E354", {"start": v(25.9, 31.25) * mm, "end": v(12.2, 31.25) * mm});
            skLineSegment(sketch, "E355", {"start": v(12.2, 31.25) * mm, "end": v(12.2, 44.95) * mm});
            skLineSegment(sketch, "E356", {"start": v(31.25, 44.95) * mm, "end": v(44.95, 44.95) * mm});
            skLineSegment(sketch, "E357", {"start": v(44.95, 44.95) * mm, "end": v(44.95, 31.25) * mm});
            skLineSegment(sketch, "E358", {"start": v(44.95, 31.25) * mm, "end": v(31.25, 31.25) * mm});
            skLineSegment(sketch, "E359", {"start": v(31.25, 31.25) * mm, "end": v(31.25, 44.95) * mm});
            skLineSegment(sketch, "E360", {"start": v(50.3, 44.95) * mm, "end": v(64, 44.95) * mm});
            skLineSegment(sketch, "E361", {"start": v(64, 44.95) * mm, "end": v(64, 31.25) * mm});
            skLineSegment(sketch, "E362", {"start": v(64, 31.25) * mm, "end": v(50.3, 31.25) * mm});
            skLineSegment(sketch, "E363", {"start": v(50.3, 31.25) * mm, "end": v(50.3, 44.95) * mm});
            skLineSegment(sketch, "E364", {"start": v(69.35, 44.95) * mm, "end": v(83.05, 44.95) * mm});
            skLineSegment(sketch, "E365", {"start": v(83.05, 44.95) * mm, "end": v(83.05, 31.25) * mm});
            skLineSegment(sketch, "E366", {"start": v(83.05, 31.25) * mm, "end": v(69.35, 31.25) * mm});
            skLineSegment(sketch, "E367", {"start": v(69.35, 31.25) * mm, "end": v(69.35, 44.95) * mm});
            skLineSegment(sketch, "E368", {"start": v(88.4, 44.95) * mm, "end": v(102.1, 44.95) * mm});
            skLineSegment(sketch, "E369", {"start": v(102.1, 44.95) * mm, "end": v(102.1, 31.25) * mm});
            skLineSegment(sketch, "E370", {"start": v(102.1, 31.25) * mm, "end": v(88.4, 31.25) * mm});
            skLineSegment(sketch, "E371", {"start": v(88.4, 31.25) * mm, "end": v(88.4, 44.95) * mm});
            skLineSegment(sketch, "E372.bottom", {"start": v(143, 51) * mm, "end": v(-143, 51) * mm});
            skLineSegment(sketch, "E372.top", {"start": v(143, -51) * mm, "end": v(-143, -51) * mm});
            skLineSegment(sketch, "E372.left", {"start": v(146, 48) * mm, "end": v(146, -48) * mm});
            skLineSegment(sketch, "E372.right", {"start": v(-146, 48) * mm, "end": v(-146, -48) * mm});
            skPoint(sketch, "E372.middle", {"position": v(0, 0) * mm});
            skPoint(sketch, "E373.visualSharp", {"position": v(-146, 51) * mm});
            skArc(sketch, "E373.filletArc", {"start": v(-143, 51) * mm, "mid": v(-145.12, 50.12) * mm, "end": v(-146, 48) * mm});
            skPoint(sketch, "E374.visualSharp", {"position": v(-146, -51) * mm});
            skArc(sketch, "E374.filletArc", {"start": v(-146, -48) * mm, "mid": v(-145.12, -50.12) * mm, "end": v(-143, -51) * mm});
            skPoint(sketch, "E375.visualSharp", {"position": v(146, -51) * mm});
            skArc(sketch, "E375.filletArc", {"start": v(143, -51) * mm, "mid": v(145.12, -50.12) * mm, "end": v(146, -48) * mm});
            skPoint(sketch, "E376.visualSharp", {"position": v(146, 51) * mm});
            skArc(sketch, "E376.filletArc", {"start": v(146, 48) * mm, "mid": v(145.12, 50.12) * mm, "end": v(143, 51) * mm});
            skSolve(sketch);
        }
        {
            var Q0;
            Q0 = qSketchRegion(id + "F0", true);
            extrude(context, id + "F1", {"entities" : qUnion([Q0]), "depth" : 5 * mm});
        }
        {
            var Q0;
            Q0=makeQuery(id+"F1.opExtrude","CAP_FACE",FACE,{"disambiguationData":[OSD([sQuery(id+"F0.wireOp",EDGE,"E0"),sQuery(id+"F0.wireOp",EDGE,"E1"),sQuery(id+"F0.wireOp",EDGE,"E2"),sQuery(id+"F0.wireOp",EDGE,"E3"),sQuery(id+"F0.wireOp",EDGE,"E4"),sQuery(id+"F0.wireOp",EDGE,"E5"),sQuery(id+"F0.wireOp",EDGE,"E6"),sQuery(id+"F0.wireOp",EDGE,"E7"),sQuery(id+"F0.wireOp",EDGE,"E8"),sQuery(id+"F0.wireOp",EDGE,"E9"),sQuery(id+"F0.wireOp",EDGE,"E10"),sQuery(id+"F0.wireOp",EDGE,"E11"),sQuery(id+"F0.wireOp",EDGE,"E12"),sQuery(id+"F0.wireOp",EDGE,"E13"),sQuery(id+"F0.wireOp",EDGE,"E14"),sQuery(id+"F0.wireOp",EDGE,"E15"),sQuery(id+"F0.wireOp",EDGE,"E16"),sQuery(id+"F0.wireOp",EDGE,"E17"),sQuery(id+"F0.wireOp",EDGE,"E18"),sQuery(id+"F0.wireOp",EDGE,"E19"),sQuery(id+"F0.wireOp",EDGE,"E20"),sQuery(id+"F0.wireOp",EDGE,"E21"),sQuery(id+"F0.wireOp",EDGE,"E22"),sQuery(id+"F0.wireOp",EDGE,"E23"),sQuery(id+"F0.wireOp",EDGE,"E24"),sQuery(id+"F0.wireOp",EDGE,"E25"),sQuery(id+"F0.wireOp",EDGE,"E26"),sQuery(id+"F0.wireOp",EDGE,"E27"),sQuery(id+"F0.wireOp",EDGE,"E28"),sQuery(id+"F0.wireOp",EDGE,"E29"),sQuery(id+"F0.wireOp",EDGE,"E30"),sQuery(id+"F0.wireOp",EDGE,"E31"),sQuery(id+"F0.wireOp",EDGE,"E32"),sQuery(id+"F0.wireOp",EDGE,"E33"),sQuery(id+"F0.wireOp",EDGE,"E34"),sQuery(id+"F0.wireOp",EDGE,"E35"),sQuery(id+"F0.wireOp",EDGE,"E36"),sQuery(id+"F0.wireOp",EDGE,"E37"),sQuery(id+"F0.wireOp",EDGE,"E38"),sQuery(id+"F0.wireOp",EDGE,"E39"),sQuery(id+"F0.wireOp",EDGE,"E40"),sQuery(id+"F0.wireOp",EDGE,"E41"),sQuery(id+"F0.wireOp",EDGE,"E42"),sQuery(id+"F0.wireOp",EDGE,"E43"),sQuery(id+"F0.wireOp",EDGE,"E44"),sQuery(id+"F0.wireOp",EDGE,"E45"),sQuery(id+"F0.wireOp",EDGE,"E46"),sQuery(id+"F0.wireOp",EDGE,"E47"),sQuery(id+"F0.wireOp",EDGE,"E48"),sQuery(id+"F0.wireOp",EDGE,"E49"),sQuery(id+"F0.wireOp",EDGE,"E50"),sQuery(id+"F0.wireOp",EDGE,"E51"),sQuery(id+"F0.wireOp",EDGE,"E52"),sQuery(id+"F0.wireOp",EDGE,"E53"),sQuery(id+"F0.wireOp",EDGE,"E54"),sQuery(id+"F0.wireOp",EDGE,"E55"),sQuery(id+"F0.wireOp",EDGE,"E56"),sQuery(id+"F0.wireOp",EDGE,"E57"),sQuery(id+"F0.wireOp",EDGE,"E58"),sQuery(id+"F0.wireOp",EDGE,"E59"),sQuery(id+"F0.wireOp",EDGE,"E60"),sQuery(id+"F0.wireOp",EDGE,"E61"),sQuery(id+"F0.wireOp",EDGE,"E62"),sQuery(id+"F0.wireOp",EDGE,"E63"),sQuery(id+"F0.wireOp",EDGE,"E64"),sQuery(id+"F0.wireOp",EDGE,"E65"),sQuery(id+"F0.wireOp",EDGE,"E66"),sQuery(id+"F0.wireOp",EDGE,"E67"),sQuery(id+"F0.wireOp",EDGE,"E68"),sQuery(id+"F0.wireOp",EDGE,"E69"),sQuery(id+"F0.wireOp",EDGE,"E70"),sQuery(id+"F0.wireOp",EDGE,"E71"),sQuery(id+"F0.wireOp",EDGE,"E72"),sQuery(id+"F0.wireOp",EDGE,"E73"),sQuery(id+"F0.wireOp",EDGE,"E74"),sQuery(id+"F0.wireOp",EDGE,"E75"),sQuery(id+"F0.wireOp",EDGE,"E76"),sQuery(id+"F0.wireOp",EDGE,"E77"),sQuery(id+"F0.wireOp",EDGE,"E78"),sQuery(id+"F0.wireOp",EDGE,"E79"),sQuery(id+"F0.wireOp",EDGE,"E80"),sQuery(id+"F0.wireOp",EDGE,"E81"),sQuery(id+"F0.wireOp",EDGE,"E82"),sQuery(id+"F0.wireOp",EDGE,"E83"),sQuery(id+"F0.wireOp",EDGE,"E84"),sQuery(id+"F0.wireOp",EDGE,"E85"),sQuery(id+"F0.wireOp",EDGE,"E86"),sQuery(id+"F0.wireOp",EDGE,"E87"),sQuery(id+"F0.wireOp",EDGE,"E88"),sQuery(id+"F0.wireOp",EDGE,"E89"),sQuery(id+"F0.wireOp",EDGE,"E90"),sQuery(id+"F0.wireOp",EDGE,"E91"),sQuery(id+"F0.wireOp",EDGE,"E92"),sQuery(id+"F0.wireOp",EDGE,"E93"),sQuery(id+"F0.wireOp",EDGE,"E94"),sQuery(id+"F0.wireOp",EDGE,"E95"),sQuery(id+"F0.wireOp",EDGE,"E96"),sQuery(id+"F0.wireOp",EDGE,"E97"),sQuery(id+"F0.wireOp",EDGE,"E98"),sQuery(id+"F0.wireOp",EDGE,"E99"),sQuery(id+"F0.wireOp",EDGE,"E100"),sQuery(id+"F0.wireOp",EDGE,"E101"),sQuery(id+"F0.wireOp",EDGE,"E102"),sQuery(id+"F0.wireOp",EDGE,"E103"),sQuery(id+"F0.wireOp",EDGE,"E104"),sQuery(id+"F0.wireOp",EDGE,"E105"),sQuery(id+"F0.wireOp",EDGE,"E106"),sQuery(id+"F0.wireOp",EDGE,"E107"),sQuery(id+"F0.wireOp",EDGE,"E108"),sQuery(id+"F0.wireOp",EDGE,"E109"),sQuery(id+"F0.wireOp",EDGE,"E110"),sQuery(id+"F0.wireOp",EDGE,"E111"),sQuery(id+"F0.wireOp",EDGE,"E112"),sQuery(id+"F0.wireOp",EDGE,"E113"),sQuery(id+"F0.wireOp",EDGE,"E114"),sQuery(id+"F0.wireOp",EDGE,"E115"),sQuery(id+"F0.wireOp",EDGE,"E116"),sQuery(id+"F0.wireOp",EDGE,"E117"),sQuery(id+"F0.wireOp",EDGE,"E118"),sQuery(id+"F0.wireOp",EDGE,"E119"),sQuery(id+"F0.wireOp",EDGE,"E120"),sQuery(id+"F0.wireOp",EDGE,"E121"),sQuery(id+"F0.wireOp",EDGE,"E122"),sQuery(id+"F0.wireOp",EDGE,"E123"),sQuery(id+"F0.wireOp",EDGE,"E124"),sQuery(id+"F0.wireOp",EDGE,"E125"),sQuery(id+"F0.wireOp",EDGE,"E126"),sQuery(id+"F0.wireOp",EDGE,"E127"),sQuery(id+"F0.wireOp",EDGE,"E128"),sQuery(id+"F0.wireOp",EDGE,"E129"),sQuery(id+"F0.wireOp",EDGE,"E130"),sQuery(id+"F0.wireOp",EDGE,"E131"),sQuery(id+"F0.wireOp",EDGE,"E132"),sQuery(id+"F0.wireOp",EDGE,"E133"),sQuery(id+"F0.wireOp",EDGE,"E134"),sQuery(id+"F0.wireOp",EDGE,"E135"),sQuery(id+"F0.wireOp",EDGE,"E136"),sQuery(id+"F0.wireOp",EDGE,"E137"),sQuery(id+"F0.wireOp",EDGE,"E138"),sQuery(id+"F0.wireOp",EDGE,"E139"),sQuery(id+"F0.wireOp",EDGE,"E140"),sQuery(id+"F0.wireOp",EDGE,"E141"),sQuery(id+"F0.wireOp",EDGE,"E142"),sQuery(id+"F0.wireOp",EDGE,"E143"),sQuery(id+"F0.wireOp",EDGE,"E144"),sQuery(id+"F0.wireOp",EDGE,"E145"),sQuery(id+"F0.wireOp",EDGE,"E146"),sQuery(id+"F0.wireOp",EDGE,"E147"),sQuery(id+"F0.wireOp",EDGE,"E148"),sQuery(id+"F0.wireOp",EDGE,"E149"),sQuery(id+"F0.wireOp",EDGE,"E150"),sQuery(id+"F0.wireOp",EDGE,"E151"),sQuery(id+"F0.wireOp",EDGE,"E152"),sQuery(id+"F0.wireOp",EDGE,"E153"),sQuery(id+"F0.wireOp",EDGE,"E154"),sQuery(id+"F0.wireOp",EDGE,"E155"),sQuery(id+"F0.wireOp",EDGE,"E156"),sQuery(id+"F0.wireOp",EDGE,"E157"),sQuery(id+"F0.wireOp",EDGE,"E158"),sQuery(id+"F0.wireOp",EDGE,"E159"),sQuery(id+"F0.wireOp",EDGE,"E160"),sQuery(id+"F0.wireOp",EDGE,"E161"),sQuery(id+"F0.wireOp",EDGE,"E162"),sQuery(id+"F0.wireOp",EDGE,"E163"),sQuery(id+"F0.wireOp",EDGE,"E164"),sQuery(id+"F0.wireOp",EDGE,"E165"),sQuery(id+"F0.wireOp",EDGE,"E166"),sQuery(id+"F0.wireOp",EDGE,"E167"),sQuery(id+"F0.wireOp",EDGE,"E168"),sQuery(id+"F0.wireOp",EDGE,"E169"),sQuery(id+"F0.wireOp",EDGE,"E170"),sQuery(id+"F0.wireOp",EDGE,"E171"),sQuery(id+"F0.wireOp",EDGE,"E172"),sQuery(id+"F0.wireOp",EDGE,"E173"),sQuery(id+"F0.wireOp",EDGE,"E174"),sQuery(id+"F0.wireOp",EDGE,"E175"),sQuery(id+"F0.wireOp",EDGE,"E176"),sQuery(id+"F0.wireOp",EDGE,"E177"),sQuery(id+"F0.wireOp",EDGE,"E178"),sQuery(id+"F0.wireOp",EDGE,"E179"),sQuery(id+"F0.wireOp",EDGE,"E180"),sQuery(id+"F0.wireOp",EDGE,"E181"),sQuery(id+"F0.wireOp",EDGE,"E182"),sQuery(id+"F0.wireOp",EDGE,"E183"),sQuery(id+"F0.wireOp",EDGE,"E184"),sQuery(id+"F0.wireOp",EDGE,"E185"),sQuery(id+"F0.wireOp",EDGE,"E186"),sQuery(id+"F0.wireOp",EDGE,"E187"),sQuery(id+"F0.wireOp",EDGE,"E188"),sQuery(id+"F0.wireOp",EDGE,"E189"),sQuery(id+"F0.wireOp",EDGE,"E190"),sQuery(id+"F0.wireOp",EDGE,"E191"),sQuery(id+"F0.wireOp",EDGE,"E192"),sQuery(id+"F0.wireOp",EDGE,"E193"),sQuery(id+"F0.wireOp",EDGE,"E194"),sQuery(id+"F0.wireOp",EDGE,"E195"),sQuery(id+"F0.wireOp",EDGE,"E196"),sQuery(id+"F0.wireOp",EDGE,"E197"),sQuery(id+"F0.wireOp",EDGE,"E198"),sQuery(id+"F0.wireOp",EDGE,"E199"),sQuery(id+"F0.wireOp",EDGE,"E200"),sQuery(id+"F0.wireOp",EDGE,"E201"),sQuery(id+"F0.wireOp",EDGE,"E202"),sQuery(id+"F0.wireOp",EDGE,"E203"),sQuery(id+"F0.wireOp",EDGE,"E204"),sQuery(id+"F0.wireOp",EDGE,"E205"),sQuery(id+"F0.wireOp",EDGE,"E206"),sQuery(id+"F0.wireOp",EDGE,"E207"),sQuery(id+"F0.wireOp",EDGE,"E208"),sQuery(id+"F0.wireOp",EDGE,"E209"),sQuery(id+"F0.wireOp",EDGE,"E210"),sQuery(id+"F0.wireOp",EDGE,"E211"),sQuery(id+"F0.wireOp",EDGE,"E212"),sQuery(id+"F0.wireOp",EDGE,"E213"),sQuery(id+"F0.wireOp",EDGE,"E214"),sQuery(id+"F0.wireOp",EDGE,"E215"),sQuery(id+"F0.wireOp",EDGE,"E216"),sQuery(id+"F0.wireOp",EDGE,"E217"),sQuery(id+"F0.wireOp",EDGE,"E218"),sQuery(id+"F0.wireOp",EDGE,"E219"),sQuery(id+"F0.wireOp",EDGE,"E220"),sQuery(id+"F0.wireOp",EDGE,"E221"),sQuery(id+"F0.wireOp",EDGE,"E222"),sQuery(id+"F0.wireOp",EDGE,"E223"),sQuery(id+"F0.wireOp",EDGE,"E224"),sQuery(id+"F0.wireOp",EDGE,"E225"),sQuery(id+"F0.wireOp",EDGE,"E226"),sQuery(id+"F0.wireOp",EDGE,"E227"),sQuery(id+"F0.wireOp",EDGE,"E228"),sQuery(id+"F0.wireOp",EDGE,"E229"),sQuery(id+"F0.wireOp",EDGE,"E230"),sQuery(id+"F0.wireOp",EDGE,"E231"),sQuery(id+"F0.wireOp",EDGE,"E232"),sQuery(id+"F0.wireOp",EDGE,"E233"),sQuery(id+"F0.wireOp",EDGE,"E234"),sQuery(id+"F0.wireOp",EDGE,"E235"),sQuery(id+"F0.wireOp",EDGE,"E236"),sQuery(id+"F0.wireOp",EDGE,"E237"),sQuery(id+"F0.wireOp",EDGE,"E238"),sQuery(id+"F0.wireOp",EDGE,"E239"),sQuery(id+"F0.wireOp",EDGE,"E240"),sQuery(id+"F0.wireOp",EDGE,"E241"),sQuery(id+"F0.wireOp",EDGE,"E242"),sQuery(id+"F0.wireOp",EDGE,"E243"),sQuery(id+"F0.wireOp",EDGE,"E244"),sQuery(id+"F0.wireOp",EDGE,"E245"),sQuery(id+"F0.wireOp",EDGE,"E246"),sQuery(id+"F0.wireOp",EDGE,"E247"),sQuery(id+"F0.wireOp",EDGE,"E248"),sQuery(id+"F0.wireOp",EDGE,"E249"),sQuery(id+"F0.wireOp",EDGE,"E250"),sQuery(id+"F0.wireOp",EDGE,"E251"),sQuery(id+"F0.wireOp",EDGE,"E252"),sQuery(id+"F0.wireOp",EDGE,"E253"),sQuery(id+"F0.wireOp",EDGE,"E254"),sQuery(id+"F0.wireOp",EDGE,"E255"),sQuery(id+"F0.wireOp",EDGE,"E256"),sQuery(id+"F0.wireOp",EDGE,"E257"),sQuery(id+"F0.wireOp",EDGE,"E258"),sQuery(id+"F0.wireOp",EDGE,"E259"),sQuery(id+"F0.wireOp",EDGE,"E260"),sQuery(id+"F0.wireOp",EDGE,"E261"),sQuery(id+"F0.wireOp",EDGE,"E262"),sQuery(id+"F0.wireOp",EDGE,"E263"),sQuery(id+"F0.wireOp",EDGE,"E264"),sQuery(id+"F0.wireOp",EDGE,"E265"),sQuery(id+"F0.wireOp",EDGE,"E266"),sQuery(id+"F0.wireOp",EDGE,"E267"),sQuery(id+"F0.wireOp",EDGE,"E268"),sQuery(id+"F0.wireOp",EDGE,"E269"),sQuery(id+"F0.wireOp",EDGE,"E270"),sQuery(id+"F0.wireOp",EDGE,"E271"),sQuery(id+"F0.wireOp",EDGE,"E272"),sQuery(id+"F0.wireOp",EDGE,"E273"),sQuery(id+"F0.wireOp",EDGE,"E274"),sQuery(id+"F0.wireOp",EDGE,"E275"),sQuery(id+"F0.wireOp",EDGE,"E276"),sQuery(id+"F0.wireOp",EDGE,"E277"),sQuery(id+"F0.wireOp",EDGE,"E278"),sQuery(id+"F0.wireOp",EDGE,"E279"),sQuery(id+"F0.wireOp",EDGE,"E280"),sQuery(id+"F0.wireOp",EDGE,"E281"),sQuery(id+"F0.wireOp",EDGE,"E282"),sQuery(id+"F0.wireOp",EDGE,"E283"),sQuery(id+"F0.wireOp",EDGE,"E284"),sQuery(id+"F0.wireOp",EDGE,"E285"),sQuery(id+"F0.wireOp",EDGE,"E286"),sQuery(id+"F0.wireOp",EDGE,"E287"),sQuery(id+"F0.wireOp",EDGE,"E288"),sQuery(id+"F0.wireOp",EDGE,"E289"),sQuery(id+"F0.wireOp",EDGE,"E290"),sQuery(id+"F0.wireOp",EDGE,"E291"),sQuery(id+"F0.wireOp",EDGE,"E292"),sQuery(id+"F0.wireOp",EDGE,"E293"),sQuery(id+"F0.wireOp",EDGE,"E294"),sQuery(id+"F0.wireOp",EDGE,"E295"),sQuery(id+"F0.wireOp",EDGE,"E296"),sQuery(id+"F0.wireOp",EDGE,"E297"),sQuery(id+"F0.wireOp",EDGE,"E298"),sQuery(id+"F0.wireOp",EDGE,"E299"),sQuery(id+"F0.wireOp",EDGE,"E300"),sQuery(id+"F0.wireOp",EDGE,"E301"),sQuery(id+"F0.wireOp",EDGE,"E302"),sQuery(id+"F0.wireOp",EDGE,"E303"),sQuery(id+"F0.wireOp",EDGE,"E304"),sQuery(id+"F0.wireOp",EDGE,"E305"),sQuery(id+"F0.wireOp",EDGE,"E306"),sQuery(id+"F0.wireOp",EDGE,"E307"),sQuery(id+"F0.wireOp",EDGE,"E308"),sQuery(id+"F0.wireOp",EDGE,"E309"),sQuery(id+"F0.wireOp",EDGE,"E310"),sQuery(id+"F0.wireOp",EDGE,"E311"),sQuery(id+"F0.wireOp",EDGE,"E312"),sQuery(id+"F0.wireOp",EDGE,"E313"),sQuery(id+"F0.wireOp",EDGE,"E314"),sQuery(id+"F0.wireOp",EDGE,"E315"),sQuery(id+"F0.wireOp",EDGE,"E316"),sQuery(id+"F0.wireOp",EDGE,"E317"),sQuery(id+"F0.wireOp",EDGE,"E318"),sQuery(id+"F0.wireOp",EDGE,"E319"),sQuery(id+"F0.wireOp",EDGE,"E320"),sQuery(id+"F0.wireOp",EDGE,"E321"),sQuery(id+"F0.wireOp",EDGE,"E322"),sQuery(id+"F0.wireOp",EDGE,"E323"),sQuery(id+"F0.wireOp",EDGE,"E324"),sQuery(id+"F0.wireOp",EDGE,"E325"),sQuery(id+"F0.wireOp",EDGE,"E326"),sQuery(id+"F0.wireOp",EDGE,"E327"),sQuery(id+"F0.wireOp",EDGE,"E328"),sQuery(id+"F0.wireOp",EDGE,"E329"),sQuery(id+"F0.wireOp",EDGE,"E330"),sQuery(id+"F0.wireOp",EDGE,"E331"),sQuery(id+"F0.wireOp",EDGE,"E332"),sQuery(id+"F0.wireOp",EDGE,"E333"),sQuery(id+"F0.wireOp",EDGE,"E334"),sQuery(id+"F0.wireOp",EDGE,"E335"),sQuery(id+"F0.wireOp",EDGE,"E336"),sQuery(id+"F0.wireOp",EDGE,"E337"),sQuery(id+"F0.wireOp",EDGE,"E338"),sQuery(id+"F0.wireOp",EDGE,"E339"),sQuery(id+"F0.wireOp",EDGE,"E340"),sQuery(id+"F0.wireOp",EDGE,"E341"),sQuery(id+"F0.wireOp",EDGE,"E342"),sQuery(id+"F0.wireOp",EDGE,"E343"),sQuery(id+"F0.wireOp",EDGE,"E344"),sQuery(id+"F0.wireOp",EDGE,"E345"),sQuery(id+"F0.wireOp",EDGE,"E346"),sQuery(id+"F0.wireOp",EDGE,"E347"),sQuery(id+"F0.wireOp",EDGE,"E348"),sQuery(id+"F0.wireOp",EDGE,"E349"),sQuery(id+"F0.wireOp",EDGE,"E350"),sQuery(id+"F0.wireOp",EDGE,"E351"),sQuery(id+"F0.wireOp",EDGE,"E352"),sQuery(id+"F0.wireOp",EDGE,"E353"),sQuery(id+"F0.wireOp",EDGE,"E354"),sQuery(id+"F0.wireOp",EDGE,"E355"),sQuery(id+"F0.wireOp",EDGE,"E356"),sQuery(id+"F0.wireOp",EDGE,"E357"),sQuery(id+"F0.wireOp",EDGE,"E358"),sQuery(id+"F0.wireOp",EDGE,"E359"),sQuery(id+"F0.wireOp",EDGE,"E360"),sQuery(id+"F0.wireOp",EDGE,"E361"),sQuery(id+"F0.wireOp",EDGE,"E362"),sQuery(id+"F0.wireOp",EDGE,"E363"),sQuery(id+"F0.wireOp",EDGE,"E364"),sQuery(id+"F0.wireOp",EDGE,"E365"),sQuery(id+"F0.wireOp",EDGE,"E366"),sQuery(id+"F0.wireOp",EDGE,"E367"),sQuery(id+"F0.wireOp",EDGE,"E368"),sQuery(id+"F0.wireOp",EDGE,"E369"),sQuery(id+"F0.wireOp",EDGE,"E370"),sQuery(id+"F0.wireOp",EDGE,"E371"),sQuery(id+"F0.wireOp",EDGE,"E372.bottom"),sQuery(id+"F0.wireOp",EDGE,"E372.top"),sQuery(id+"F0.wireOp",EDGE,"E372.left"),sQuery(id+"F0.wireOp",EDGE,"E372.right")])],"isStart":false});
            var sketch = newSketch(context, id + "F2", { "sketchPlane" : qUnion([Q0])});
            skCircle(sketch, "E377", {"center": v(-142, 47) * mm, "radius": 1.1 * mm});
            skCircle(sketch, "E378", {"center": v(142, 47) * mm, "radius": 1.1 * mm});
            skCircle(sketch, "E379", {"center": v(-66.83, 47) * mm, "radius": 1.1 * mm});
            skCircle(sketch, "E380", {"center": v(66.17, 47) * mm, "radius": 1.1 * mm});
            skCircle(sketch, "E381", {"center": v(-142, -47) * mm, "radius": 1.1 * mm});
            skCircle(sketch, "E382", {"center": v(142, -47) * mm, "radius": 1.1 * mm});
            skCircle(sketch, "E383", {"center": v(-71, -47) * mm, "radius": 1.1 * mm});
            skCircle(sketch, "E384", {"center": v(46, -47) * mm, "radius": 1.1 * mm});
            skCircle(sketch, "E385", {"center": v(142, 3) * mm, "radius": 1.1 * mm});
            skCircle(sketch, "E386", {"center": v(-142, 3) * mm, "radius": 1.1 * mm});
            skCircle(sketch, "E387", {"center": v(105.17, 47) * mm, "radius": 1.1 * mm});
            skSolve(sketch);
        }
        {
            var Q0;
            Q0 = qSketchRegion(id + "F2", true);
            extrude(context, id + "F3", {"entities" : qUnion([Q0]), "operationType" : NewBodyOperationType.REMOVE, "endBound" : BoundingType.THROUGH_ALL, "oppositeDirection" : true, "depth" : 25 * mm});
        }
    });
